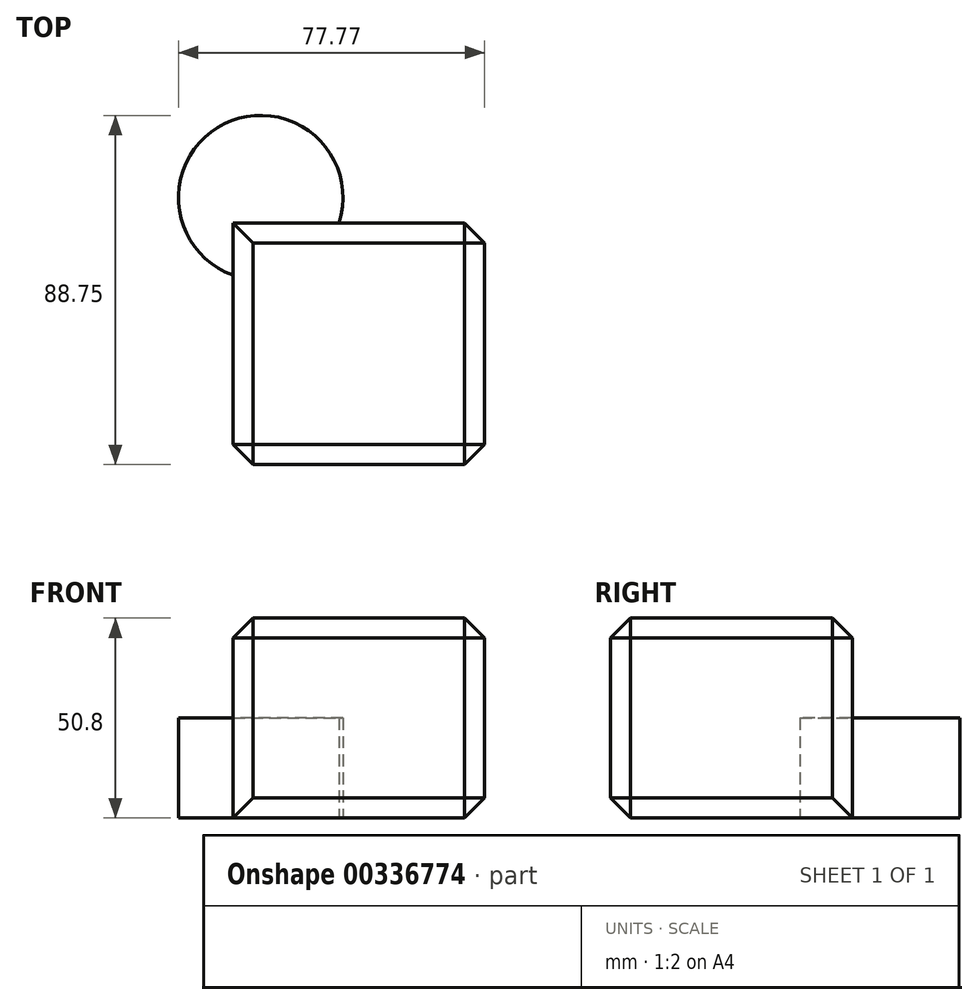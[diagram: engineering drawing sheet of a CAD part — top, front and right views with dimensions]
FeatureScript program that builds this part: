
annotation { "Feature Type Name" : "Feature", "Feature Type Description" : "" }
export const myFeature = defineFeature(function(context is Context, id is Id, definition is map)
    precondition{}
    {
        {
            var Q0;
            Q0=qCreatedBy(makeId("Top.planeOp"),FACE);
            var sketch = newSketch(context, id + "F0", { "sketchPlane" : qUnion([Q0])});
            skLineSegment(sketch, "E0.bottom", {"start": v(-39.69, -28.64) * mm, "end": v(24.2, -28.64) * mm});
            skLineSegment(sketch, "E0.top", {"start": v(-39.69, 32.79) * mm, "end": v(24.2, 32.79) * mm});
            skLineSegment(sketch, "E0.left", {"start": v(-39.69, -28.64) * mm, "end": v(-39.69, 32.79) * mm});
            skLineSegment(sketch, "E0.right", {"start": v(24.2, -28.64) * mm, "end": v(24.2, 32.79) * mm});
            skSolve(sketch);
        }
        {
            var Q0;
            Q0 = qSketchRegion(id + "F0", true);
            extrude(context, id + "F1", {"entities" : qUnion([Q0]), "depth" : 25.4 * mm});
        }
        {
            var Q0;
            Q0=qCreatedBy(makeId("Top.planeOp"),FACE);
            var sketch = newSketch(context, id + "F2", { "sketchPlane" : qUnion([Q0])});
            skCircle(sketch, "E1", {"center": v(-32.66, 39.2) * mm, "radius": 20.9 * mm});
            skSolve(sketch);
        }
        {
            var Q0;
            Q0=makeQuery(id+"F2.imprint","IMPRINT",FACE,{"disambiguationData":[TD([[makeQuery(id+"F2.imprint","IMPRINT",EDGE,{"derivedFrom":sQuery(id+"F2.wireOp",EDGE,"E1")}),1.0]])]});
            var Q1;
            Q1=makeQuery(id+"F1.opExtrude","CAP_FACE",FACE,{"disambiguationData":[OSD([sQuery(id+"F0.wireOp",EDGE,"E0.bottom"),sQuery(id+"F0.wireOp",EDGE,"E0.top"),sQuery(id+"F0.wireOp",EDGE,"E0.left"),sQuery(id+"F0.wireOp",EDGE,"E0.right")])],"isStart":false});
            extrude(context, id + "F3", {"entities" : qUnion([Q0, Q1]), "operationType" : NewBodyOperationType.ADD, "depth" : 25.4 * mm});
        }
        {
            var Q0;
            {var subQ0=sQuery(id+"F0.wireOp",EDGE,"E0.bottom");Q0=makeQuery(id+"F3.boolean.opBoolean","MERGE",FACE,{"derivedFrom":[makeQuery(id+"F1.opExtrude","SWEPT_FACE",FACE,{"disambiguationData":[OSD([subQ0])]}),makeQuery(id+"F3.opExtrude","SWEPT_FACE",FACE,{"disambiguationData":[OSD([subQ0])]})]});}
            var Q1;
            {var subQ0=sQuery(id+"F0.wireOp",EDGE,"E0.right");Q1=makeQuery(id+"F3.boolean.opBoolean","MERGE",FACE,{"derivedFrom":[makeQuery(id+"F1.opExtrude","SWEPT_FACE",FACE,{"disambiguationData":[OSD([subQ0])]}),makeQuery(id+"F3.opExtrude","SWEPT_FACE",FACE,{"disambiguationData":[OSD([subQ0])]})]});}
            var Q2;
            Q2=makeQuery(id+"F3.opExtrude","CAP_FACE",FACE,{"disambiguationData":[OSD([sQuery(id+"F0.wireOp",EDGE,"E0.bottom"),sQuery(id+"F0.wireOp",EDGE,"E0.top"),sQuery(id+"F0.wireOp",EDGE,"E0.left"),sQuery(id+"F0.wireOp",EDGE,"E0.right")])],"isStart":false});
            var Q3;
            Q3=makeQuery(id+"F3.opExtrude","CAP_EDGE",EDGE,{"disambiguationData":[OSD([sQuery(id+"F0.wireOp",EDGE,"E0.bottom")])],"isStart":false});
            chamfer(context, id + "F4", {"entities" : qUnion([Q0, Q1, Q2, Q3]), "width" : 5.08 * mm, "tangentPropagation" : true});
        }
    });
